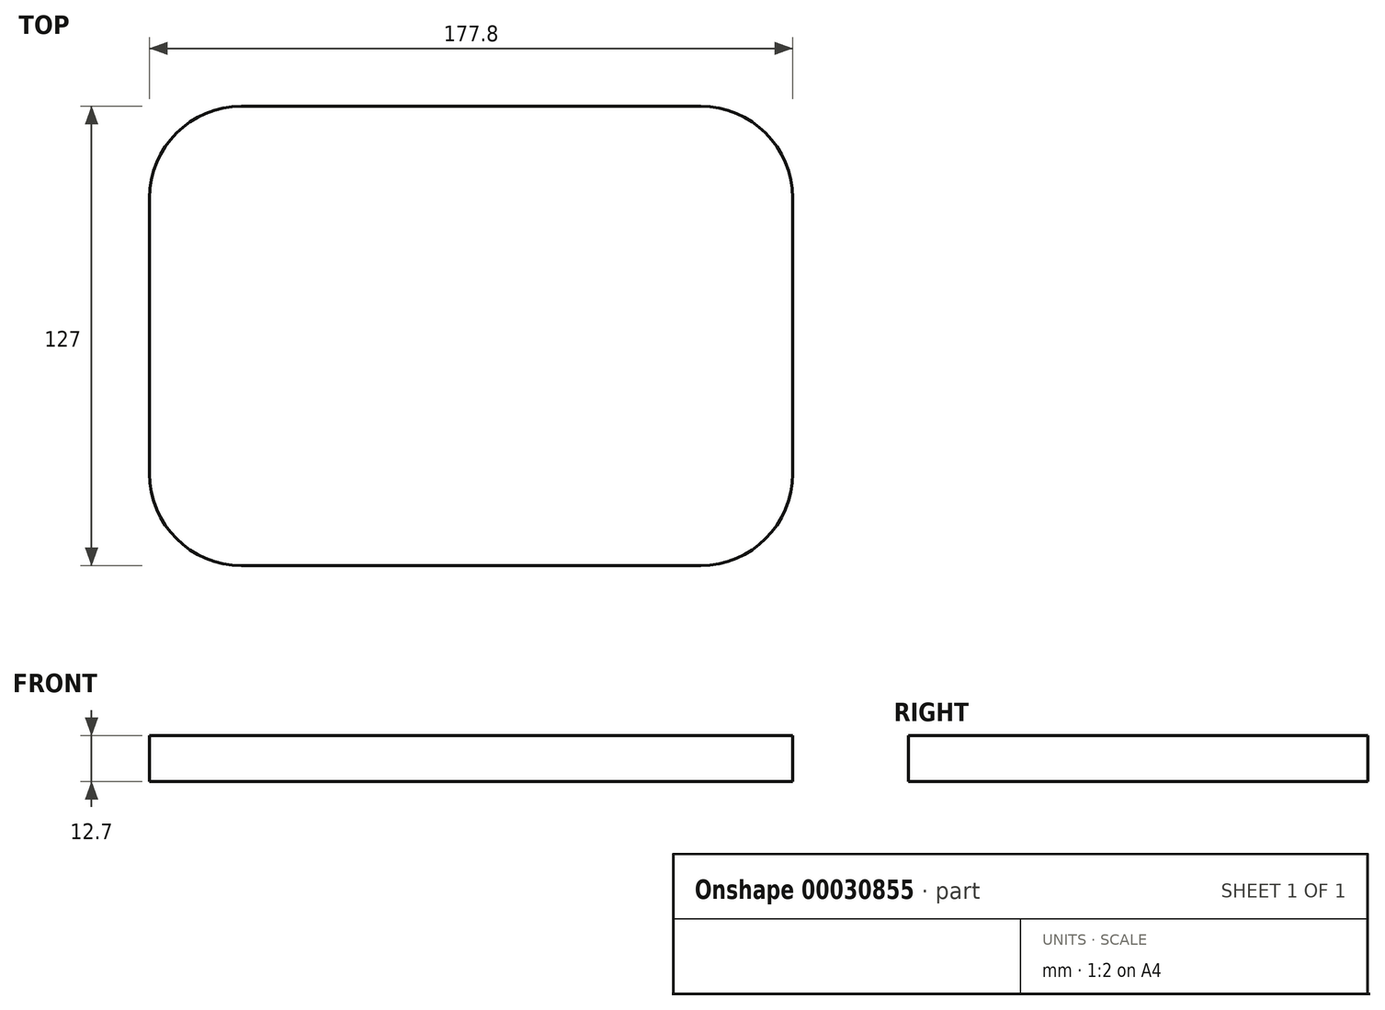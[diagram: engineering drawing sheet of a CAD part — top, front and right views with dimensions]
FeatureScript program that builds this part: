
annotation { "Feature Type Name" : "Feature", "Feature Type Description" : "" }
export const myFeature = defineFeature(function(context is Context, id is Id, definition is map)
    precondition{}
    {
        {
            var Q0;
            Q0=qCreatedBy(makeId("Top.planeOp"),FACE);
            var sketch = newSketch(context, id + "F0", { "sketchPlane" : qUnion([Q0])});
            skLineSegment(sketch, "E0", {"start": v(0, 0) * mm, "end": v(0, -38.61) * mm});
            skLineSegment(sketch, "E1", {"start": v(0, 0) * mm, "end": v(0, 37.59) * mm});
            skLineSegment(sketch, "E2", {"start": v(-25.4, -64.01) * mm, "end": v(-152.4, -64.01) * mm});
            skLineSegment(sketch, "E3", {"start": v(-25.4, 62.99) * mm, "end": v(-152.4, 62.99) * mm});
            skLineSegment(sketch, "E4", {"start": v(-177.8, 37.59) * mm, "end": v(-177.8, -38.61) * mm});
            skPoint(sketch, "E5.visualSharp", {"position": v(-177.8, -64.01) * mm});
            skArc(sketch, "E5.filletArc", {"start": v(-177.8, -38.61) * mm, "mid": v(-170.36, -56.57) * mm, "end": v(-152.4, -64.01) * mm});
            skPoint(sketch, "E6.visualSharp", {"position": v(-177.8, 62.99) * mm});
            skArc(sketch, "E6.filletArc", {"start": v(-152.4, 62.99) * mm, "mid": v(-170.36, 55.55) * mm, "end": v(-177.8, 37.59) * mm});
            skPoint(sketch, "E7.visualSharp", {"position": v(0, 62.99) * mm});
            skArc(sketch, "E7.filletArc", {"start": v(0, 37.59) * mm, "mid": v(-7.44, 55.55) * mm, "end": v(-25.4, 62.99) * mm});
            skPoint(sketch, "E8.visualSharp", {"position": v(0, -64.01) * mm});
            skArc(sketch, "E8.filletArc", {"start": v(-25.4, -64.01) * mm, "mid": v(-7.44, -56.57) * mm, "end": v(0, -38.61) * mm});
            skSolve(sketch);
        }
        {
            var Q0;
            Q0 = qSketchRegion(id + "F0", true);
            extrude(context, id + "F1", {"entities" : qUnion([Q0]), "depth" : 12.7 * mm});
        }
    });
